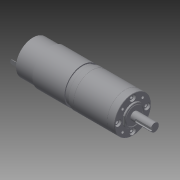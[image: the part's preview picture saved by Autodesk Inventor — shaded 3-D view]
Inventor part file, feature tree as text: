
AUTODESK INVENTOR PART (.ipt)
format: ipt  version: 2014 (Build 180170000, 170)  size: 352,768 bytes
history: native  units: in
note: dims shown in document units (in); Inventor stores cm internally (conversion verified against a paired STEP export)
features: mirror x1, other x1, imported_body x1
ambient origin geometry x8: Origin, YZ Plane, XZ Plane, XY Plane, X Axis, Y Axis, Z Axis, Center Point
bodies: Body1 (feature_tree)
feature tree (3):
  mirror  "Mirror2"
  other  "PG-71-am-09141"
  imported_body  "Base1"
